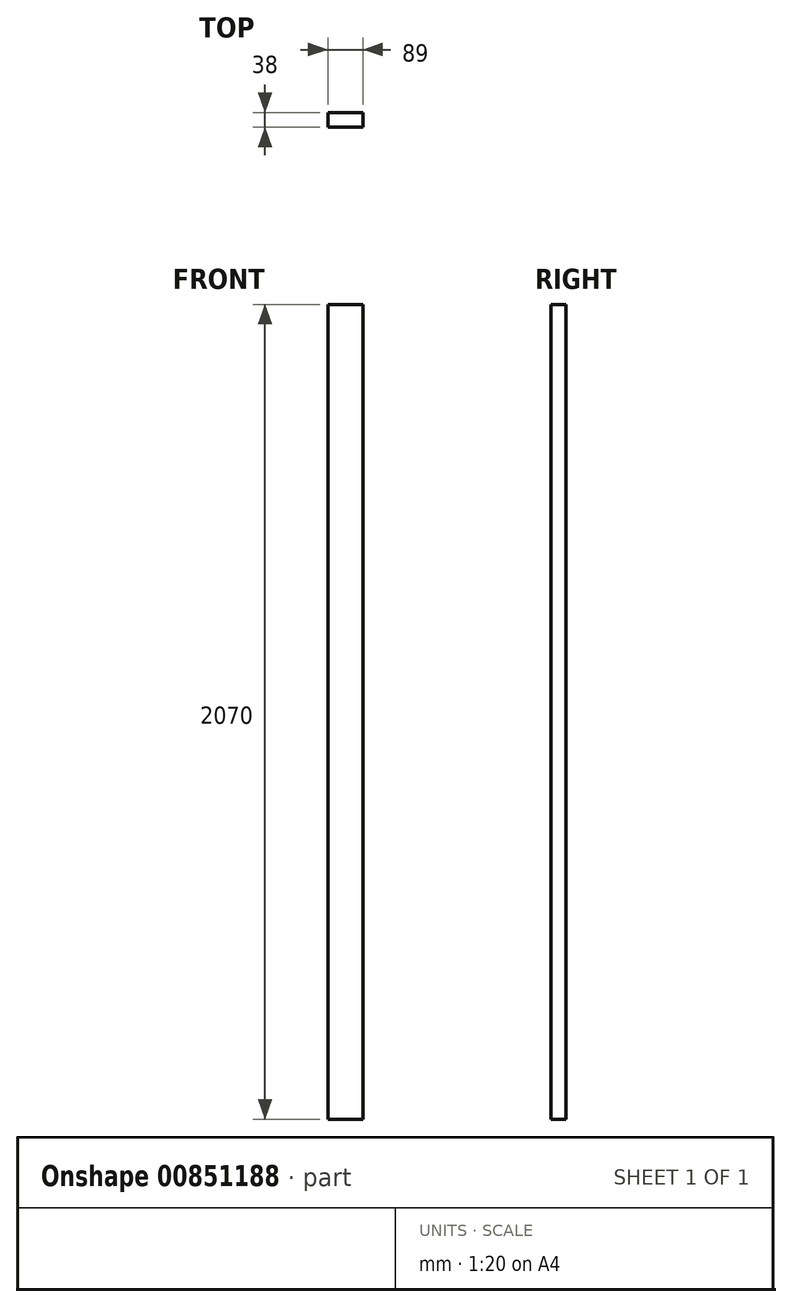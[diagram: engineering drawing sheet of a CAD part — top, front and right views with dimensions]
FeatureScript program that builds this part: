
annotation { "Feature Type Name" : "Feature", "Feature Type Description" : "" }
export const myFeature = defineFeature(function(context is Context, id is Id, definition is map)
    precondition{}
    {
        {
            var Q0;
            Q0=qCreatedBy(makeId("Top.planeOp"),FACE);
            var sketch = newSketch(context, id + "F0", { "sketchPlane" : qUnion([Q0])});
            skLineSegment(sketch, "E0.bottom", {"start": v(0, -19) * mm, "end": v(44.5, -19) * mm});
            skLineSegment(sketch, "E0.right", {"start": v(44.5, -19) * mm, "end": v(44.5, 19) * mm});
            skLineSegment(sketch, "E1", {"start": v(0, -19) * mm, "end": v(-44.5, -19) * mm});
            skLineSegment(sketch, "E2", {"start": v(-44.5, -19) * mm, "end": v(-44.5, 19) * mm});
            skLineSegment(sketch, "E3", {"start": v(44.5, 19) * mm, "end": v(-44.5, 19) * mm});
            skSolve(sketch);
        }
        {
            var Q0;
            Q0 = qSketchRegion(id + "F0", true);
            extrude(context, id + "F1", {"entities" : qUnion([Q0]), "depth" : (2130 - 60) * mm, "offsetDistance" : 25 * mm});
        }
    });
